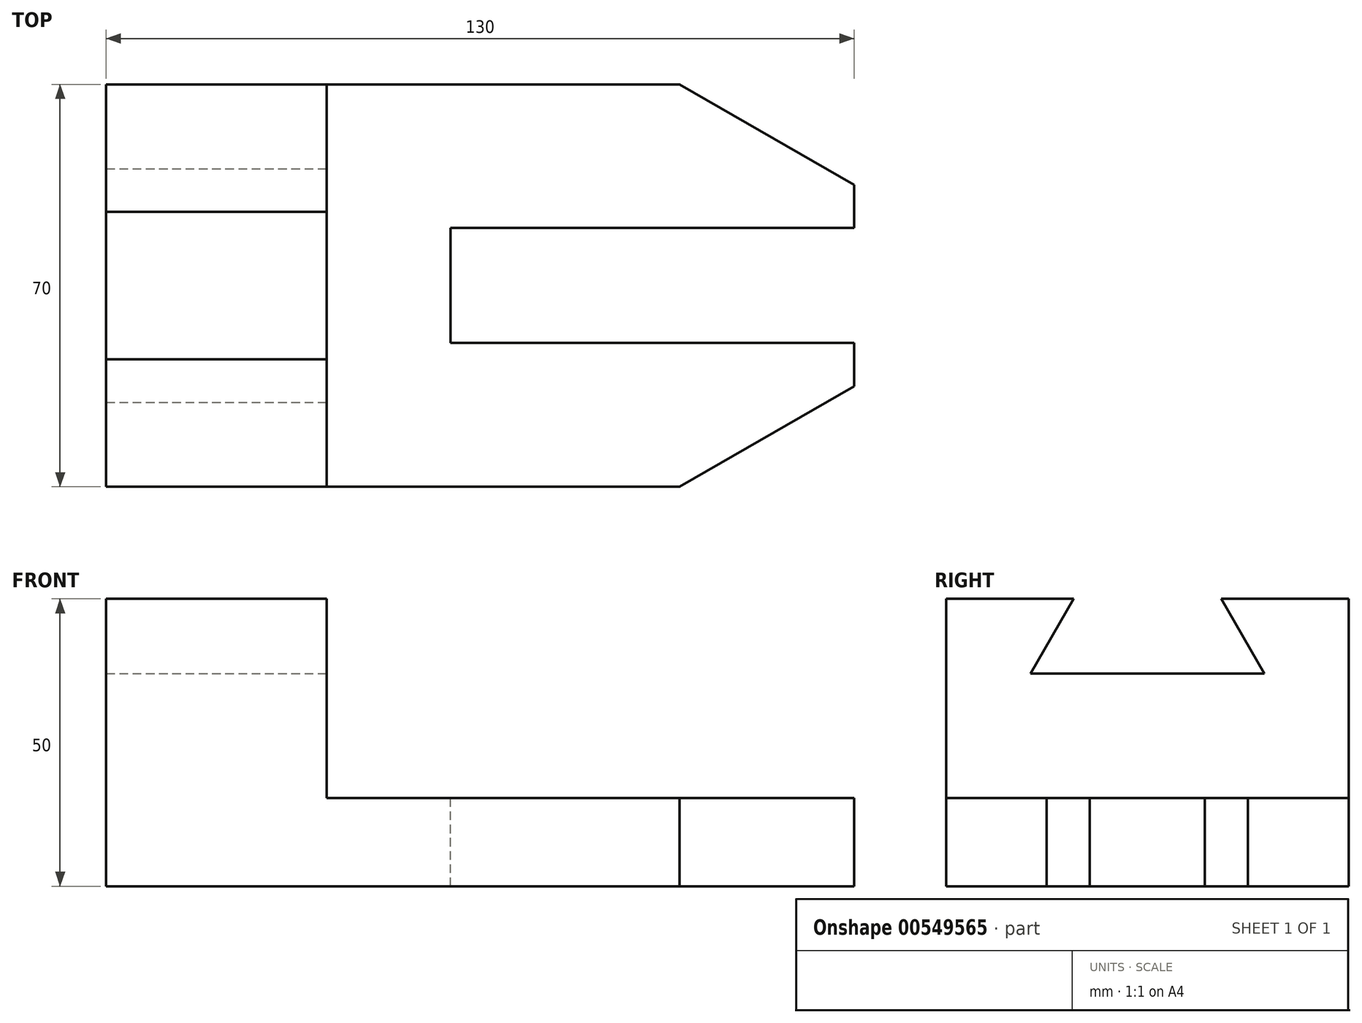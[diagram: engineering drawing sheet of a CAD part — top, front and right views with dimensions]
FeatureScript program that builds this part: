
annotation { "Feature Type Name" : "Feature", "Feature Type Description" : "" }
export const myFeature = defineFeature(function(context is Context, id is Id, definition is map)
    precondition{}
    {
        {
            var Q0;
            Q0=qCreatedBy(makeId("Front.planeOp"),FACE);
            var sketch = newSketch(context, id + "F0", { "sketchPlane" : qUnion([Q0])});
            skLineSegment(sketch, "E0", {"start": v(-51.36, 34.63) * mm, "end": v(-51.36, -15.37) * mm});
            skLineSegment(sketch, "E1", {"start": v(-51.36, -15.37) * mm, "end": v(78.64, -15.37) * mm});
            skLineSegment(sketch, "E2", {"start": v(78.64, -15.37) * mm, "end": v(78.64, 0) * mm});
            skLineSegment(sketch, "E3", {"start": v(78.64, 0) * mm, "end": v(-13.04, 0) * mm});
            skLineSegment(sketch, "E4", {"start": v(-13.04, 0) * mm, "end": v(-13.04, 34.63) * mm});
            skLineSegment(sketch, "E5", {"start": v(-13.04, 34.63) * mm, "end": v(-51.36, 34.63) * mm});
            skSolve(sketch);
        }
        {
            var Q0;
            Q0=makeQuery(id+"F0.imprint","IMPRINT",FACE,{"disambiguationData":[TD([[makeQuery(id+"F0.imprint","IMPRINT",EDGE,{"derivedFrom":sQuery(id+"F0.wireOp",EDGE,"E0")}),1.0]])]});
            extrude(context, id + "F1", {"entities" : qUnion([Q0]), "depth" : 70 * mm, "offsetDistance" : 25 * mm});
        }
        {
            var Q0;
            Q0=makeQuery(id+"F1.opExtrude","SWEPT_FACE",FACE,{"disambiguationData":[OSD([sQuery(id+"F0.wireOp",EDGE,"E4")])]});
            var sketch = newSketch(context, id + "F2", { "sketchPlane" : qUnion([Q0])});
            skLineSegment(sketch, "E6", {"start": v(-70, 34.63) * mm, "end": v(-35, 34.63) * mm, "construction": true});
            skLineSegment(sketch, "E7", {"start": v(-35, 34.63) * mm, "end": v(0, 34.63) * mm, "construction": true});
            skLineSegment(sketch, "E8", {"start": v(-35, 34.63) * mm, "end": v(-35, 0) * mm, "construction": true});
            skLineSegment(sketch, "E9", {"start": v(-47.83, 34.63) * mm, "end": v(-55.33, 21.64) * mm});
            skLineSegment(sketch, "E10", {"start": v(-55.33, 21.64) * mm, "end": v(-35, 21.64) * mm});
            skLineSegment(sketch, "E11.MirrorCS", {"start": v(-14.67, 21.64) * mm, "end": v(-35, 21.64) * mm});
            skLineSegment(sketch, "E12.MirrorCS", {"start": v(-22.17, 34.63) * mm, "end": v(-14.67, 21.64) * mm});
            skSolve(sketch);
        }
        {
            var Q0;
            Q0 = qSketchRegion(id + "F2", true);
            var Q1;
            {var subQ1=sQuery(id+"F2.wireOp",EDGE,"E9");Q1=makeQuery(id+"F2.imprint","IMPRINT",FACE,{"disambiguationData":[TD([[makeQuery(id+"F2.imprint","IMPRINT",EDGE,{"derivedFrom":subQ1}),1.0]])]});}
            extrude(context, id + "F3", {"entities" : qUnion([Q0, Q1]), "operationType" : NewBodyOperationType.REMOVE, "endBound" : BoundingType.THROUGH_ALL, "oppositeDirection" : true, "depth" : 25 * mm, "offsetDistance" : 25 * mm});
        }
        {
            var Q0;
            Q0=makeQuery(id+"F1.opExtrude","SWEPT_FACE",FACE,{"disambiguationData":[OSD([sQuery(id+"F0.wireOp",EDGE,"E3")])]});
            var sketch = newSketch(context, id + "F4", { "sketchPlane" : qUnion([Q0])});
            skLineSegment(sketch, "E13", {"start": v(78.64, -70) * mm, "end": v(78.64, -45) * mm});
            skLineSegment(sketch, "E14", {"start": v(78.64, -25) * mm, "end": v(78.64, 0) * mm});
            skLineSegment(sketch, "E15", {"start": v(78.64, -45) * mm, "end": v(8.49, -45) * mm});
            skLineSegment(sketch, "E16", {"start": v(8.49, -45) * mm, "end": v(8.49, -25) * mm});
            skLineSegment(sketch, "E17", {"start": v(8.49, -25) * mm, "end": v(78.64, -25) * mm});
            skSolve(sketch);
        }
        {
            var Q0;
            Q0 = qSketchRegion(id + "F4", true);
            var Q1;
            {var subQ0=sQuery(id+"F4.wireOp",EDGE,"E15");Q1=makeQuery(id+"F4.imprint","IMPRINT",FACE,{"disambiguationData":[TD([[makeQuery(id+"F4.imprint","IMPRINT",EDGE,{"derivedFrom":subQ0}),-1.0]])]});}
            extrude(context, id + "F5", {"entities" : qUnion([Q0, Q1]), "operationType" : NewBodyOperationType.REMOVE, "endBound" : BoundingType.THROUGH_ALL, "oppositeDirection" : true, "depth" : 25 * mm, "offsetDistance" : 25 * mm});
        }
        {
            var Q0;
            Q0=makeQuery(id+"F1.opExtrude","SWEPT_FACE",FACE,{"disambiguationData":[OSD([sQuery(id+"F0.wireOp",EDGE,"E3")])]});
            var sketch = newSketch(context, id + "F6", { "sketchPlane" : qUnion([Q0])});
            skSolve(sketch);
        }
        {
            var Q0;
            Q0=makeQuery(id+"F1.opExtrude","SWEPT_FACE",FACE,{"disambiguationData":[OSD([sQuery(id+"F0.wireOp",EDGE,"E3")])]});
            var sketch = newSketch(context, id + "F7", { "sketchPlane" : qUnion([Q0])});
            skLineSegment(sketch, "E18", {"start": v(78.64, -17.5) * mm, "end": v(48.33, 0) * mm});
            skLineSegment(sketch, "E19.MirrorCS", {"start": v(78.64, -52.5) * mm, "end": v(48.33, -70) * mm});
            skSolve(sketch);
        }
        {
            var Q0;
            {var subQ0=sQuery(id+"F7.wireOp",EDGE,"E19.MirrorCS");Q0=makeQuery(id+"F7.imprint","IMPRINT",FACE,{"disambiguationData":[TD([[makeQuery(id+"F7.imprint","IMPRINT",EDGE,{"derivedFrom":subQ0}),1.0]])]});}
            var Q1;
            {var subQ0=sQuery(id+"F7.wireOp",EDGE,"E18");Q1=makeQuery(id+"F7.imprint","IMPRINT",FACE,{"disambiguationData":[TD([[makeQuery(id+"F7.imprint","IMPRINT",EDGE,{"derivedFrom":subQ0}),-1.0]])]});}
            extrude(context, id + "F8", {"entities" : qUnion([Q0, Q1]), "operationType" : NewBodyOperationType.REMOVE, "endBound" : BoundingType.THROUGH_ALL, "oppositeDirection" : true, "depth" : 25 * mm, "offsetDistance" : 25 * mm});
        }
    });
